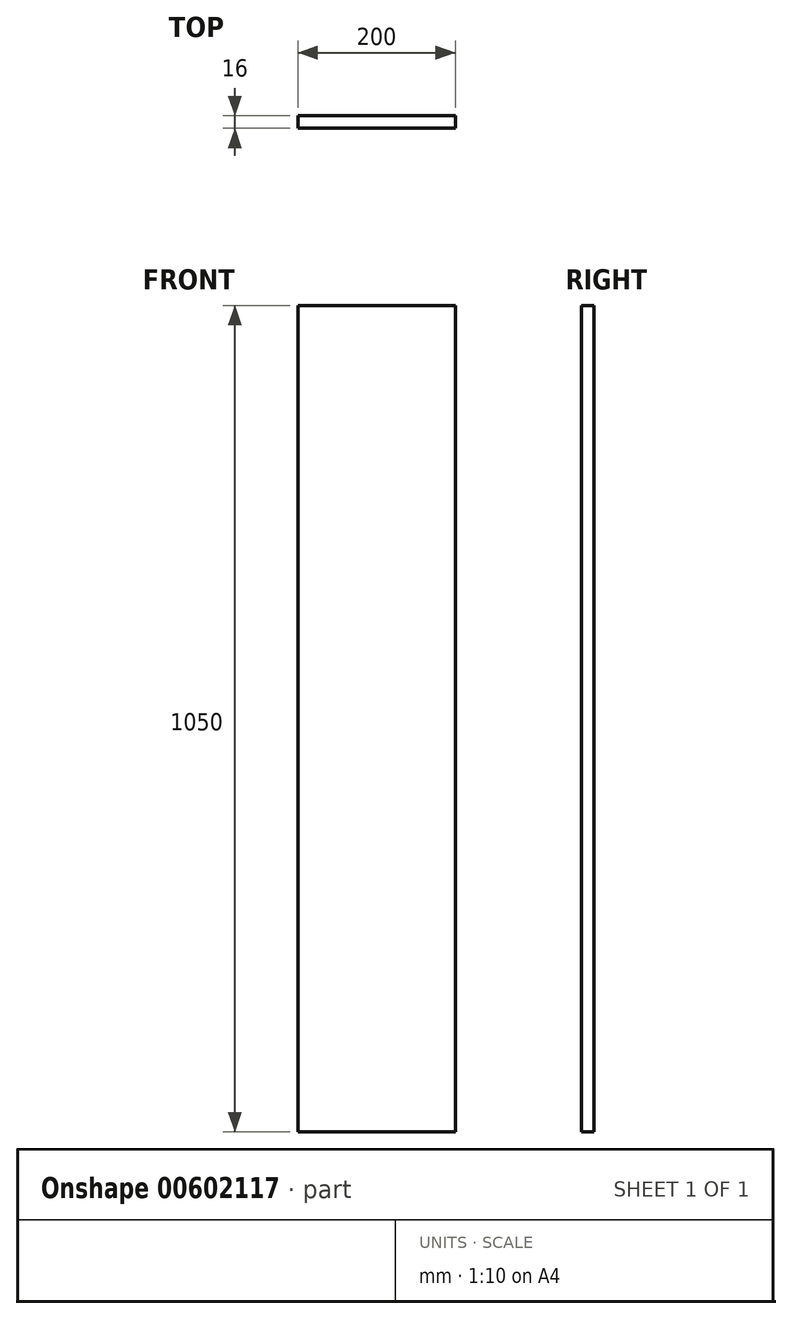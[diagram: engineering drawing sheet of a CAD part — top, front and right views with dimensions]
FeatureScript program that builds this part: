
annotation { "Feature Type Name" : "Feature", "Feature Type Description" : "" }
export const myFeature = defineFeature(function(context is Context, id is Id, definition is map)
    precondition{}
    {
        {
            var Q0;
            Q0=qCreatedBy(makeId("Front.planeOp"),FACE);
            var sketch = newSketch(context, id + "F0", { "sketchPlane" : qUnion([Q0])});
            skLineSegment(sketch, "E0.bottom", {"start": v(0, 0) * mm, "end": v(200, 0) * mm});
            skLineSegment(sketch, "E0.top", {"start": v(0, 1050) * mm, "end": v(200, 1050) * mm});
            skLineSegment(sketch, "E0.left", {"start": v(0, 0) * mm, "end": v(0, 1050) * mm});
            skLineSegment(sketch, "E0.right", {"start": v(200, 0) * mm, "end": v(200, 1050) * mm});
            skSolve(sketch);
        }
        {
            var Q0;
            Q0 = qSketchRegion(id + "F0", true);
            extrude(context, id + "F1", {"entities" : qUnion([Q0]), "depth" : 16 * mm, "offsetDistance" : 25 * mm});
        }
    });
